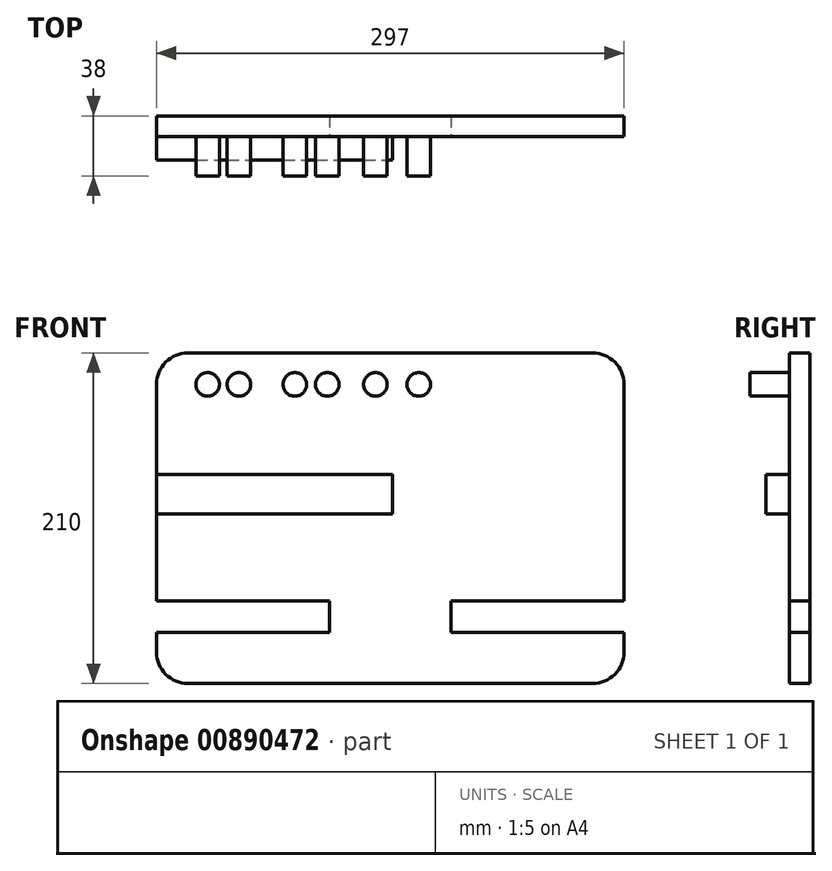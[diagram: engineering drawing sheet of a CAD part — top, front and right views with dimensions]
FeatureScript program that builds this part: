
annotation { "Feature Type Name" : "Feature", "Feature Type Description" : "" }
export const myFeature = defineFeature(function(context is Context, id is Id, definition is map)
    precondition{}
    {
        {
            var Q0;
            Q0=qCreatedBy(makeId("Front.planeOp"),FACE);
            var sketch = newSketch(context, id + "F0", { "sketchPlane" : qUnion([Q0])});
            skLineSegment(sketch, "E0.bottom", {"start": v(-123.64, 102.24) * mm, "end": v(133.36, 102.24) * mm});
            skLineSegment(sketch, "E0.top", {"start": v(-123.64, -107.76) * mm, "end": v(133.36, -107.76) * mm});
            skLineSegment(sketch, "E0.left", {"start": v(-143.64, 82.24) * mm, "end": v(-143.64, -87.76) * mm});
            skLineSegment(sketch, "E0.right", {"start": v(153.36, 82.24) * mm, "end": v(153.36, -87.76) * mm});
            skPoint(sketch, "E1.visualSharp", {"position": v(-143.64, 102.24) * mm});
            skArc(sketch, "E1.filletArc", {"start": v(-123.64, 102.24) * mm, "mid": v(-137.78, 96.38) * mm, "end": v(-143.64, 82.24) * mm});
            skPoint(sketch, "E2.visualSharp", {"position": v(153.36, 102.24) * mm});
            skArc(sketch, "E2.filletArc", {"start": v(153.36, 82.24) * mm, "mid": v(147.5, 96.38) * mm, "end": v(133.36, 102.24) * mm});
            skPoint(sketch, "E3.visualSharp", {"position": v(153.36, -107.76) * mm});
            skArc(sketch, "E3.filletArc", {"start": v(133.36, -107.76) * mm, "mid": v(147.5, -101.9) * mm, "end": v(153.36, -87.76) * mm});
            skPoint(sketch, "E4.visualSharp", {"position": v(-143.64, -107.76) * mm});
            skArc(sketch, "E4.filletArc", {"start": v(-143.64, -87.76) * mm, "mid": v(-137.78, -101.9) * mm, "end": v(-123.64, -107.76) * mm});
            skLineSegment(sketch, "E5.left", {"start": v(-143.64, -61.83) * mm, "end": v(-143.64, -81.83) * mm});
            skLineSegment(sketch, "E6.right", {"start": v(153.36, -61.83) * mm, "end": v(153.36, -81.83) * mm});
            skPoint(sketch, "E5.right.end.orphan", {"position": v(-33.64, -81.83) * mm});
            skPoint(sketch, "E5.right.start.orphan", {"position": v(-33.64, -61.83) * mm});
            skPoint(sketch, "E6.bottom.start.orphan", {"position": v(43.36, -61.83) * mm});
            skSolve(sketch);
        }
        {
            var Q0;
            Q0 = qSketchRegion(id + "F0", true);
            extrude(context, id + "F1", {"entities" : qUnion([Q0]), "depth" : 13 * mm, "offsetDistance" : 25 * mm});
        }
        {
            var Q0;
            Q0=makeQuery(id+"F1.opExtrude","CAP_FACE",FACE,{"disambiguationData":[OSD([sQuery(id+"F0.wireOp",EDGE,"E0.bottom"),sQuery(id+"F0.wireOp",EDGE,"E0.top"),sQuery(id+"F0.wireOp",EDGE,"E0.left"),sQuery(id+"F0.wireOp",EDGE,"E0.right"),sQuery(id+"F0.wireOp",EDGE,"E1.filletArc"),sQuery(id+"F0.wireOp",EDGE,"E2.filletArc"),sQuery(id+"F0.wireOp",EDGE,"E3.filletArc"),sQuery(id+"F0.wireOp",EDGE,"E4.filletArc"),sQuery(id+"F0.wireOp",EDGE,"E5.left"),sQuery(id+"F0.wireOp",EDGE,"E6.right")])],"isStart":false});
            var sketch = newSketch(context, id + "F2", { "sketchPlane" : qUnion([Q0])});
            skLineSegment(sketch, "E7.bottom", {"start": v(-143.64, -55.32) * mm, "end": v(-33.64, -55.32) * mm});
            skLineSegment(sketch, "E7.top", {"start": v(-143.64, -75.32) * mm, "end": v(-33.64, -75.32) * mm});
            skLineSegment(sketch, "E7.left", {"start": v(-143.64, -55.32) * mm, "end": v(-143.64, -75.32) * mm});
            skLineSegment(sketch, "E7.right", {"start": v(-33.64, -55.32) * mm, "end": v(-33.64, -75.32) * mm});
            skLineSegment(sketch, "E8.bottom", {"start": v(43.36, -55.32) * mm, "end": v(153.36, -55.32) * mm});
            skLineSegment(sketch, "E8.top", {"start": v(43.36, -75.32) * mm, "end": v(153.36, -75.32) * mm});
            skLineSegment(sketch, "E8.left", {"start": v(43.36, -55.32) * mm, "end": v(43.36, -75.32) * mm});
            skLineSegment(sketch, "E8.right", {"start": v(153.36, -55.32) * mm, "end": v(153.36, -75.32) * mm});
            skSolve(sketch);
        }
        {
            var Q0;
            Q0 = qSketchRegion(id + "F2", true);
            extrude(context, id + "F3", {"entities" : qUnion([Q0]), "operationType" : NewBodyOperationType.REMOVE, "oppositeDirection" : true, "depth" : 25 * mm, "offsetDistance" : 25 * mm});
        }
        {
            var Q0;
            Q0=makeQuery(id+"F1.opExtrude","CAP_FACE",FACE,{"disambiguationData":[OSD([sQuery(id+"F0.wireOp",EDGE,"E0.bottom"),sQuery(id+"F0.wireOp",EDGE,"E0.top"),sQuery(id+"F0.wireOp",EDGE,"E0.left"),sQuery(id+"F0.wireOp",EDGE,"E0.right"),sQuery(id+"F0.wireOp",EDGE,"E1.filletArc"),sQuery(id+"F0.wireOp",EDGE,"E2.filletArc"),sQuery(id+"F0.wireOp",EDGE,"E3.filletArc"),sQuery(id+"F0.wireOp",EDGE,"E4.filletArc"),sQuery(id+"F0.wireOp",EDGE,"E5.left"),sQuery(id+"F0.wireOp",EDGE,"E6.right")])],"isStart":false});
            var sketch = newSketch(context, id + "F4", { "sketchPlane" : qUnion([Q0])});
            skLineSegment(sketch, "E9.bottom", {"start": v(-143.64, 25) * mm, "end": v(6.36, 25) * mm});
            skLineSegment(sketch, "E9.top", {"start": v(-143.64, 0) * mm, "end": v(6.36, 0) * mm});
            skLineSegment(sketch, "E9.left", {"start": v(-143.64, 25) * mm, "end": v(-143.64, 0) * mm});
            skLineSegment(sketch, "E9.right", {"start": v(6.36, 25) * mm, "end": v(6.36, 0) * mm});
            skSolve(sketch);
        }
        {
            var Q0;
            Q0 = qSketchRegion(id + "F4", true);
            extrude(context, id + "F5", {"entities" : qUnion([Q0]), "operationType" : NewBodyOperationType.ADD, "depth" : 15 * mm, "offsetDistance" : 25 * mm});
        }
        {
            var Q0;
            Q0=makeQuery(id+"F1.opExtrude","CAP_FACE",FACE,{"disambiguationData":[OSD([sQuery(id+"F0.wireOp",EDGE,"E0.bottom"),sQuery(id+"F0.wireOp",EDGE,"E0.top"),sQuery(id+"F0.wireOp",EDGE,"E0.left"),sQuery(id+"F0.wireOp",EDGE,"E0.right"),sQuery(id+"F0.wireOp",EDGE,"E1.filletArc"),sQuery(id+"F0.wireOp",EDGE,"E2.filletArc"),sQuery(id+"F0.wireOp",EDGE,"E3.filletArc"),sQuery(id+"F0.wireOp",EDGE,"E4.filletArc"),sQuery(id+"F0.wireOp",EDGE,"E5.left"),sQuery(id+"F0.wireOp",EDGE,"E6.right")])],"isStart":false});
            var sketch = newSketch(context, id + "F6", { "sketchPlane" : qUnion([Q0])});
            skCircle(sketch, "E10", {"center": v(-111.14, 82.24) * mm, "radius": 7.5 * mm});
            skCircle(sketch, "E11", {"center": v(-91.27, 82.24) * mm, "radius": 7.5 * mm});
            skCircle(sketch, "E12", {"center": v(-55.74, 82.24) * mm, "radius": 7.5 * mm});
            skCircle(sketch, "E13", {"center": v(-35.15, 82.24) * mm, "radius": 7.5 * mm});
            skCircle(sketch, "E14", {"center": v(-4.6, 82.24) * mm, "radius": 7.5 * mm});
            skCircle(sketch, "E15", {"center": v(22.96, 82.24) * mm, "radius": 7.5 * mm});
            skSolve(sketch);
        }
        {
            var Q0;
            Q0 = qSketchRegion(id + "F6", true);
            extrude(context, id + "F7", {"entities" : qUnion([Q0]), "operationType" : NewBodyOperationType.ADD, "depth" : 25 * mm, "offsetDistance" : 25 * mm});
        }
    });
